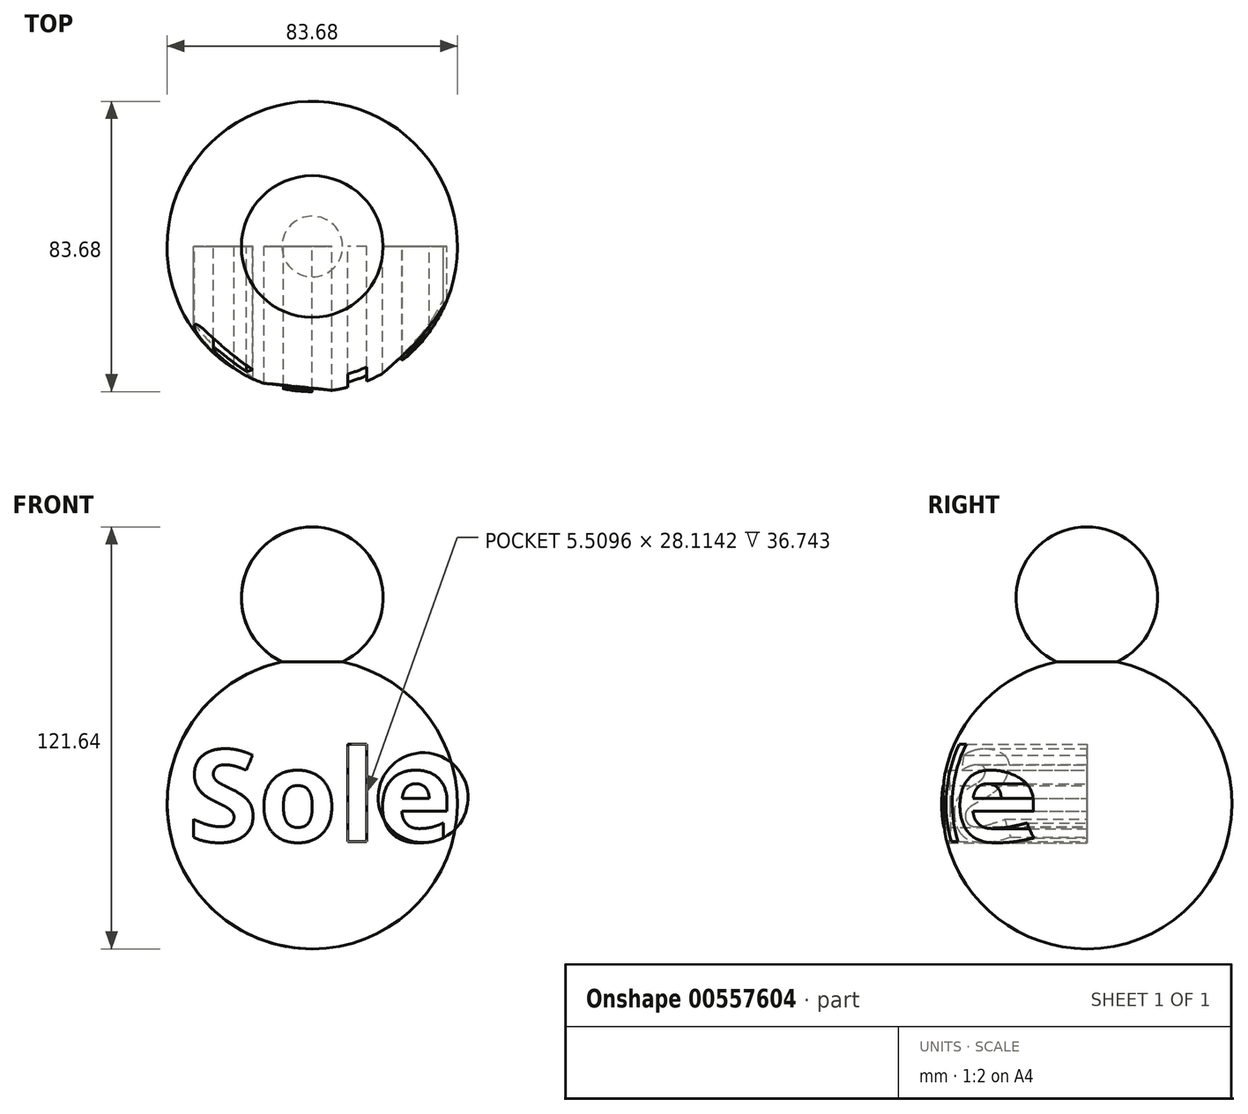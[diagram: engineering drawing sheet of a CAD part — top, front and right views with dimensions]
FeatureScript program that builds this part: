
annotation { "Feature Type Name" : "Feature", "Feature Type Description" : "" }
export const myFeature = defineFeature(function(context is Context, id is Id, definition is map)
    precondition{}
    {
        {
            var Q0;
            Q0=qCreatedBy(makeId("Front.planeOp"),FACE);
            var sketch = newSketch(context, id + "F0", { "sketchPlane" : qUnion([Q0])});
            skArc(sketch, "E0", {"start": v(-8.76, 40.91) * mm, "mid": v(-41.6, -4.4) * mm, "end": v(0, -41.84) * mm});
            skArc(sketch, "E1", {"start": v(-8.76, 40.91) * mm, "mid": v(-4.49, 39.44) * mm, "end": v(0, 38.94) * mm});
            skLineSegment(sketch, "E2", {"start": v(0, -41.84) * mm, "end": v(0, 79.8) * mm});
            skArc(sketch, "E3", {"start": v(0, 79.8) * mm, "mid": v(-20.43, 59.37) * mm, "end": v(0, 38.94) * mm});
            skLineSegment(sketch, "E4", {"start": v(0, 79.8) * mm, "end": v(0, -41.84) * mm});
            skSolve(sketch);
        }
        {
            var Q0;
            {var subQ0=sQuery(id+"F0.wireOp",EDGE,"E3");var subQ1=makeQuery(id+"F0.imprint","INTERSECT",VERTEX,{"derivedFrom":[sQuery(id+"F0.wireOp",EDGE,"E0"),subQ0]});Q0=makeQuery(id+"F0.imprint","IMPRINT",FACE,{"disambiguationData":[TD([[makeQuery(id+"F0.imprint","IMPRINT",EDGE,{"disambiguationData":[TD([[subQ1,1.0]])],"derivedFrom":subQ0}),1.0]])]});}
            var Q1;
            {var subQ0=sQuery(id+"F0.wireOp",EDGE,"E0");Q1=makeQuery(id+"F0.imprint","IMPRINT",FACE,{"disambiguationData":[TD([[makeQuery(id+"F0.imprint","IMPRINT",EDGE,{"derivedFrom":subQ0}),1.0]])]});}
            var Q2;
            Q2=sQuery(id+"F0.wireOp",EDGE,"E4");
            revolve(context, id + "F1", {"entities" : qUnion([Q0, Q1]), "axis" : qUnion([Q2]), "revolveType" : RevolveType.FULL});
        }
        {
            var Q0;
            Q0=qCreatedBy(makeId("Front.planeOp"),FACE);
            var sketch = newSketch(context, id + "F2", { "sketchPlane" : qUnion([Q0])});
            skText(sketch, "E5", { "text": "Sole ", "fontName": "OpenSans-Bold.ttf"});
            const initialGuessF2  = {"E5": [-0.03598, -0.0109, 1, 0, 0.02664]};
            skSetInitialGuess(sketch, initialGuessF2);
            skSolve(sketch);
        }
        {
            var Q0;
            Q0 = qSketchRegion(id + "F2", true);
            extrude(context, id + "F3", {"entities" : qUnion([Q0]), "operationType" : NewBodyOperationType.REMOVE, "depth" : 55.12 * mm, "offsetDistance" : 25.4 * mm});
        }
    });
